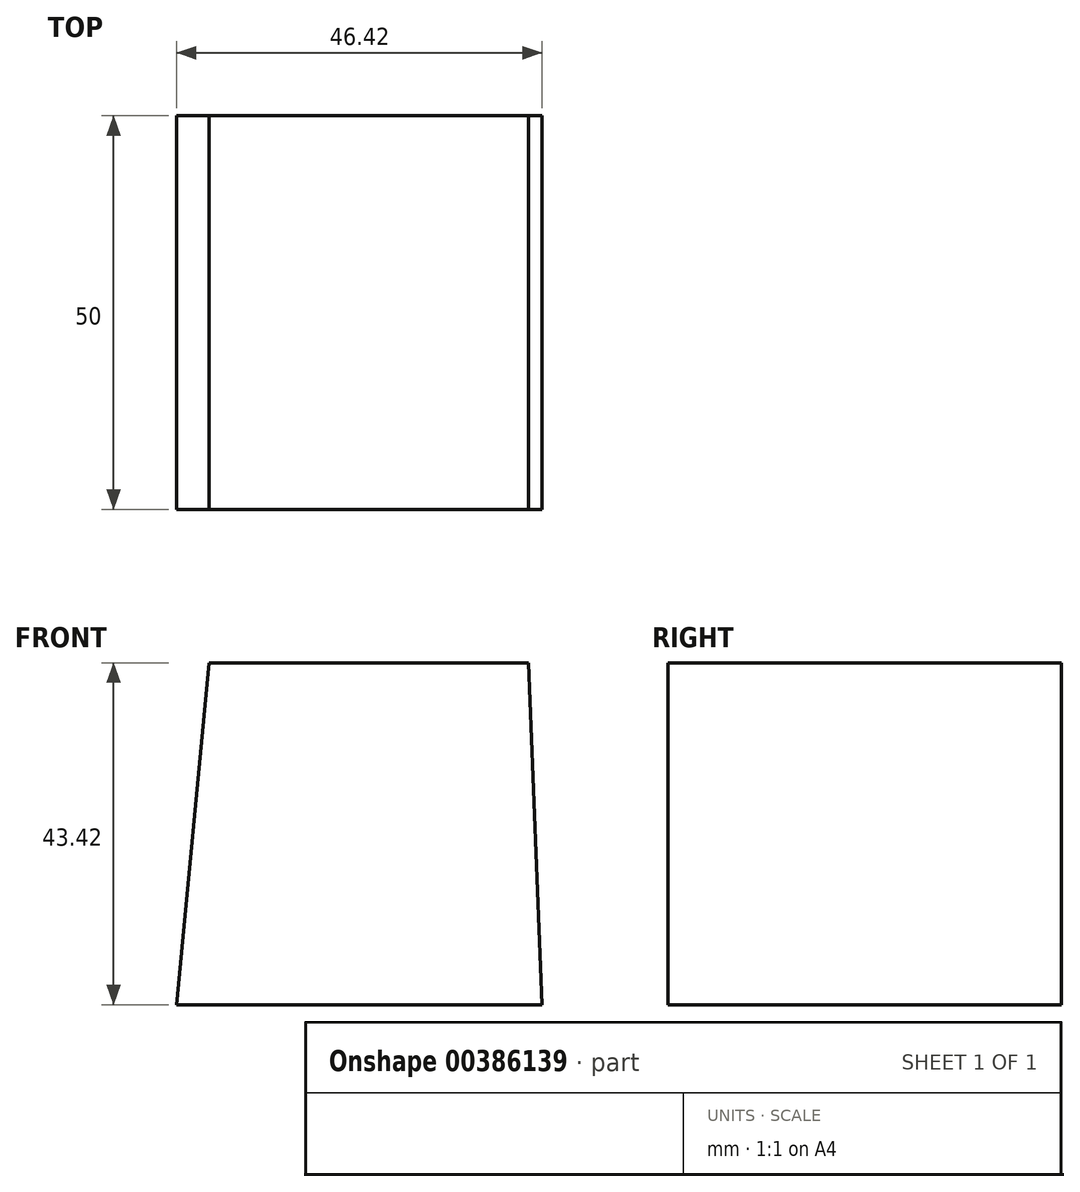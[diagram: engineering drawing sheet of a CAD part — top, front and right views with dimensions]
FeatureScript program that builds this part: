
annotation { "Feature Type Name" : "Feature", "Feature Type Description" : "" }
export const myFeature = defineFeature(function(context is Context, id is Id, definition is map)
    precondition{}
    {
        {
            var Q0;
            Q0=qCreatedBy(makeId("Front.planeOp"),FACE);
            var sketch = newSketch(context, id + "F0", { "sketchPlane" : qUnion([Q0])});
            skLineSegment(sketch, "E0", {"start": v(-19.73, 25) * mm, "end": v(20.86, 25) * mm});
            skLineSegment(sketch, "E1", {"start": v(20.86, 25) * mm, "end": v(22.55, -18.42) * mm});
            skLineSegment(sketch, "E2", {"start": v(22.55, -18.42) * mm, "end": v(-23.87, -18.42) * mm});
            skLineSegment(sketch, "E3", {"start": v(-23.87, -18.42) * mm, "end": v(-19.73, 25) * mm});
            skSolve(sketch);
        }
        {
            var Q0;
            Q0 = qSketchRegion(id + "F0", true);
            extrude(context, id + "F1", {"entities" : qUnion([Q0]), "depth" : 25 * mm});
        }
        {
            var Q0;
            Q0=qCreatedBy(makeId("Front.planeOp"),FACE);
            var sketch = newSketch(context, id + "F2", { "sketchPlane" : qUnion([Q0])});
            skCircle(sketch, "E4", {"center": v(0, 0) * mm, "radius": 6.72 * mm});
            skSolve(sketch);
        }
        {
            var Q0;
            Q0=makeQuery(id+"F1.opExtrude","CAP_FACE",FACE,{"disambiguationData":[OSD([sQuery(id+"F0.wireOp",EDGE,"E0"),sQuery(id+"F0.wireOp",EDGE,"E1"),sQuery(id+"F0.wireOp",EDGE,"E2"),sQuery(id+"F0.wireOp",EDGE,"E3")])],"isStart":false});
            extrude(context, id + "F3", {"entities" : qUnion([Q0]), "operationType" : NewBodyOperationType.ADD, "depth" : 25 * mm});
        }
        {
            var Q0;
            Q0=sQuery(id+"F2.wireOp",EDGE,"E4");
            extrude(context, id + "F4", {"bodyType" : ToolBodyType.SURFACE, "surfaceEntities" : qUnion([Q0]), "depth" : 25 * mm});
        }
    });
